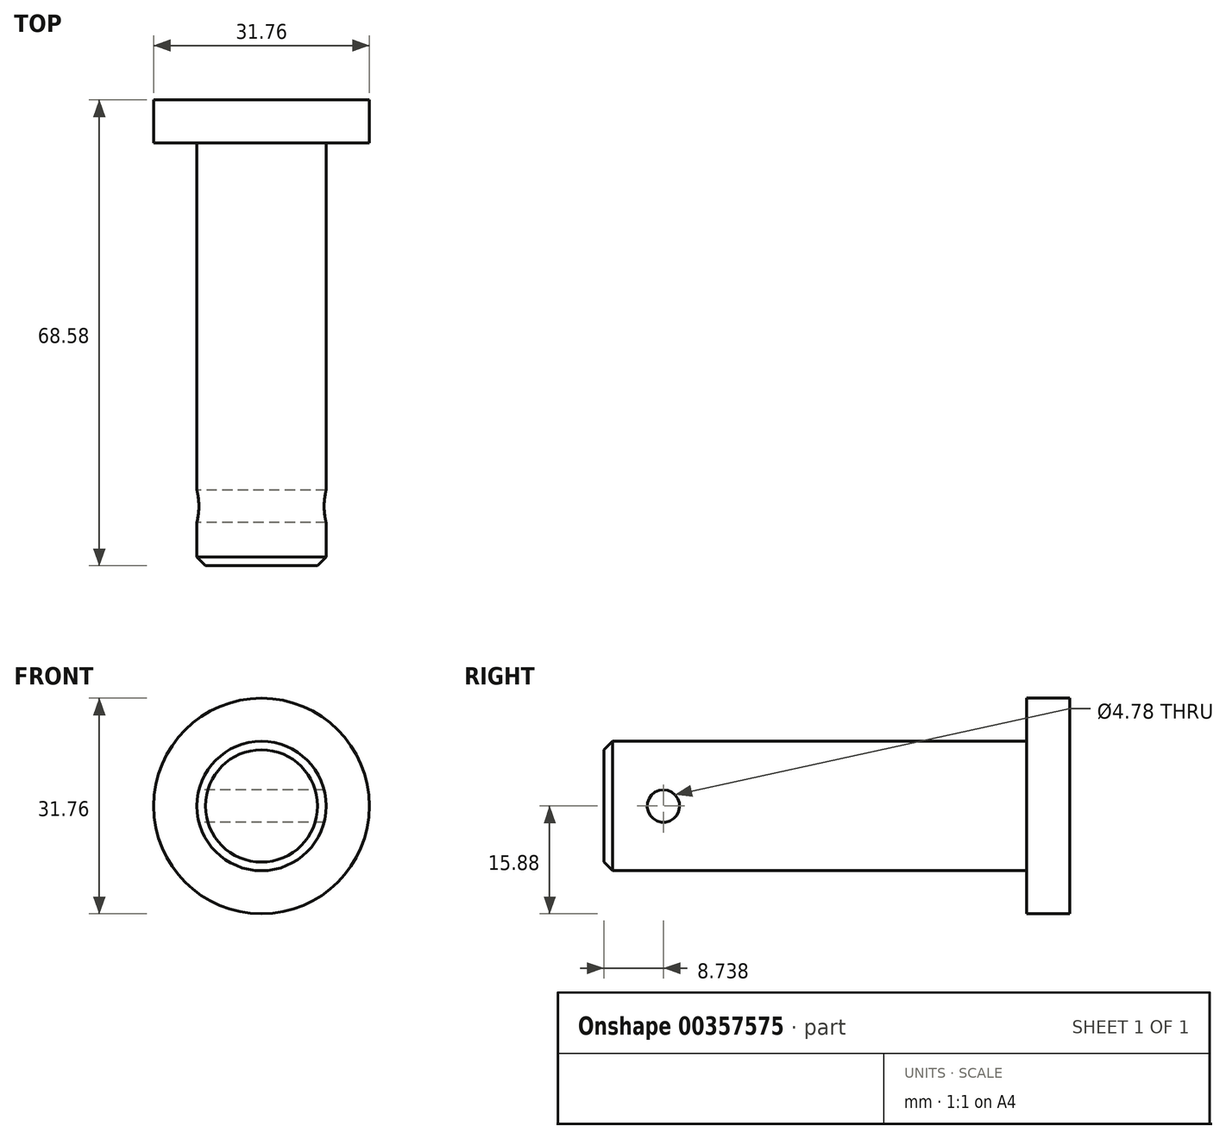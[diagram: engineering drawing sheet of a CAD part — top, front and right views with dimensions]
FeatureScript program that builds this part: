
annotation { "Feature Type Name" : "Feature", "Feature Type Description" : "" }
export const myFeature = defineFeature(function(context is Context, id is Id, definition is map)
    precondition{}
    {
        {
            var Q0;
            Q0=qCreatedBy(makeId("Front.planeOp"),FACE);
            var sketch = newSketch(context, id + "F0", { "sketchPlane" : qUnion([Q0])});
            skCircle(sketch, "E0", {"center": v(0, 0) * mm, "radius": 15.88 * mm});
            skSolve(sketch);
        }
        {
            var Q0;
            Q0 = qSketchRegion(id + "F0", true);
            extrude(context, id + "F1", {"entities" : qUnion([Q0]), "depth" : 6.35 * mm});
        }
        {
            var Q0;
            Q0=makeQuery(id+"F1.opExtrude","CAP_FACE",FACE,{"disambiguationData":[OSD([sQuery(id+"F0.wireOp",EDGE,"E0")])],"isStart":false});
            var sketch = newSketch(context, id + "F2", { "sketchPlane" : qUnion([Q0])});
            skCircle(sketch, "E1", {"center": v(0, 0) * mm, "radius": 9.53 * mm});
            skSolve(sketch);
        }
        {
            var Q0;
            Q0 = qSketchRegion(id + "F2", true);
            extrude(context, id + "F3", {"entities" : qUnion([Q0]), "operationType" : NewBodyOperationType.ADD, "depth" : 62.23 * mm});
        }
        {
            var Q0;
            Q0=qCreatedBy(makeId("Right.planeOp"),FACE);
            var sketch = newSketch(context, id + "F4", { "sketchPlane" : qUnion([Q0])});
            skCircle(sketch, "E2", {"center": v(-59.84, 0) * mm, "radius": 2.39 * mm});
            skSolve(sketch);
        }
        {
            var Q0;
            Q0 = qSketchRegion(id + "F4", true);
            extrude(context, id + "F5", {"entities" : qUnion([Q0]), "operationType" : NewBodyOperationType.REMOVE, "endBound" : BoundingType.SYMMETRIC, "depth" : 25.4 * mm});
        }
        {
            var Q0;
            Q0=makeQuery(id+"F3.opExtrude","CAP_EDGE",EDGE,{"disambiguationData":[OSD([sQuery(id+"F2.wireOp",EDGE,"E1")])],"isStart":false});
            chamfer(context, id + "F6", {"entities" : qUnion([Q0]), "chamferType" : ChamferType.OFFSET_ANGLE, "width" : 1.27 * mm, "oppositeDirection" : false, "angle" : 45 * degree, "tangentPropagation" : true});
        }
    });
